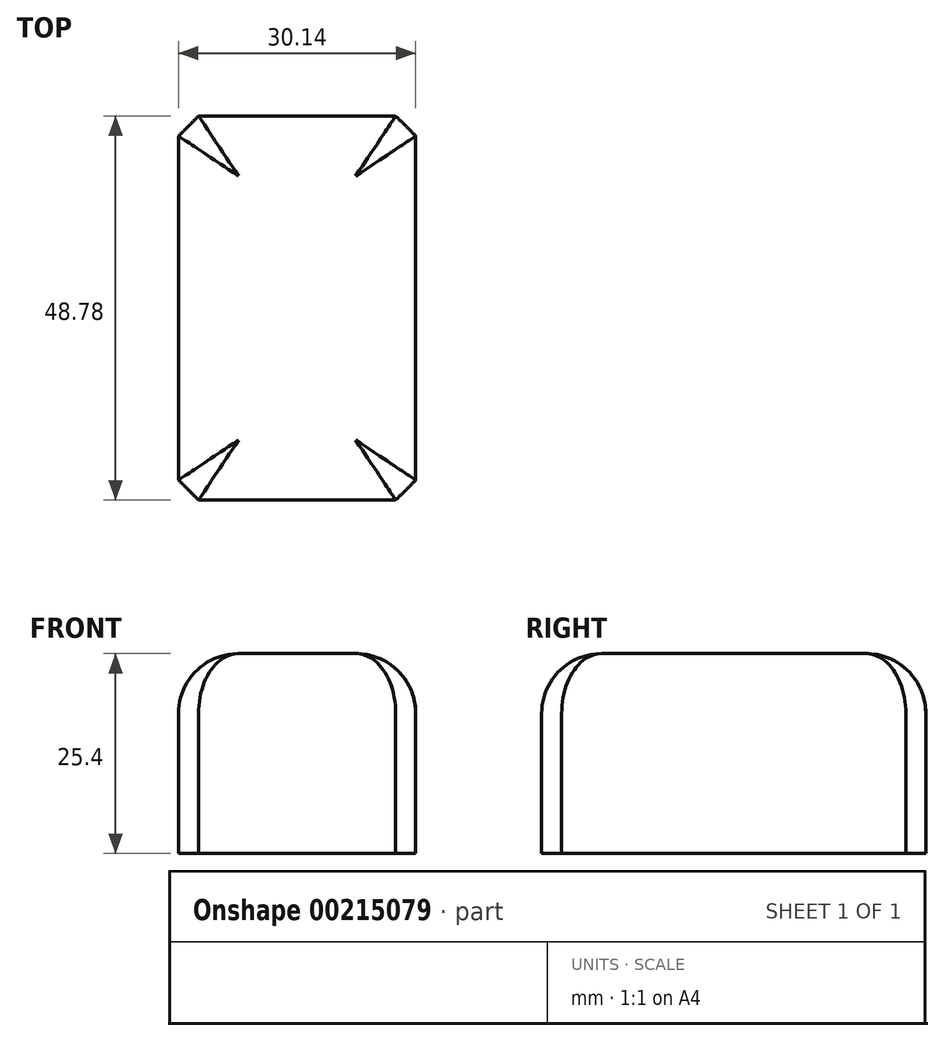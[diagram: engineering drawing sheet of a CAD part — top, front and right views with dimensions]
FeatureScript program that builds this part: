
annotation { "Feature Type Name" : "Feature", "Feature Type Description" : "" }
export const myFeature = defineFeature(function(context is Context, id is Id, definition is map)
    precondition{}
    {
        {
            var Q0;
            Q0=qCreatedBy(makeId("Top.planeOp"),FACE);
            var sketch = newSketch(context, id + "F2", { "sketchPlane" : qUnion([Q0])});
            skLineSegment(sketch, "E0.bottom", {"start": v(15.07, -24.4) * mm, "end": v(-15.07, -24.4) * mm});
            skLineSegment(sketch, "E0.top", {"start": v(15.07, 24.4) * mm, "end": v(-15.07, 24.4) * mm});
            skLineSegment(sketch, "E0.left", {"start": v(15.07, -24.4) * mm, "end": v(15.07, 24.4) * mm});
            skLineSegment(sketch, "E0.right", {"start": v(-15.07, -24.4) * mm, "end": v(-15.07, 24.4) * mm});
            skPoint(sketch, "E0.middle", {"position": v(0, 0) * mm});
            skSolve(sketch);
        }
        {
            var Q0;
            Q0=makeQuery(id+"F2.imprint","IMPRINT",FACE,{"disambiguationData":[TD([[makeQuery(id+"F2.imprint","IMPRINT",EDGE,{"derivedFrom":sQuery(id+"F2.wireOp",EDGE,"E0.bottom")}),-1.0]])]});
            extrude(context, id + "F0", {"entities" : qUnion([Q0]), "depth" : 25.4 * mm});
        }
        {
            var Q0;
            Q0=makeQuery(id+"F0.opExtrude","CAP_EDGE",EDGE,{"disambiguationData":[OSD([sQuery(id+"F2.wireOp",EDGE,"E0.left")])],"isStart":false});
            var Q1;
            Q1=makeQuery(id+"F0.opExtrude","CAP_EDGE",EDGE,{"disambiguationData":[OSD([sQuery(id+"F2.wireOp",EDGE,"E0.top")])],"isStart":false});
            var Q2;
            Q2=makeQuery(id+"F0.opExtrude","CAP_EDGE",EDGE,{"disambiguationData":[OSD([sQuery(id+"F2.wireOp",EDGE,"E0.right")])],"isStart":false});
            var Q3;
            Q3=makeQuery(id+"F0.opExtrude","CAP_EDGE",EDGE,{"disambiguationData":[OSD([sQuery(id+"F2.wireOp",EDGE,"E0.bottom")])],"isStart":false});
            fillet(context, id + "F1", {"entities" : qUnion([Q0, Q1, Q2, Q3]), "radius" : 7.62 * mm, "tangentPropagation" : true, "allowEdgeOverflow" : false});
        }
        {
            var Q0;
            Q0=makeQuery(id+"F0.opExtrude","SWEPT_EDGE",EDGE,{"disambiguationData":[OSD([sQuery(id+"F2.wireOp",EDGE,"E0.bottom"),sQuery(id+"F2.wireOp",EDGE,"E0.left")])]});
            var Q1;
            Q1=makeQuery(id+"F0.opExtrude","SWEPT_EDGE",EDGE,{"disambiguationData":[OSD([sQuery(id+"F2.wireOp",EDGE,"E0.bottom"),sQuery(id+"F2.wireOp",EDGE,"E0.right")])]});
            var Q2;
            Q2=makeQuery(id+"F0.opExtrude","SWEPT_EDGE",EDGE,{"disambiguationData":[OSD([sQuery(id+"F2.wireOp",EDGE,"E0.top"),sQuery(id+"F2.wireOp",EDGE,"E0.left")])]});
            var Q3;
            Q3=makeQuery(id+"F0.opExtrude","SWEPT_EDGE",EDGE,{"disambiguationData":[OSD([sQuery(id+"F2.wireOp",EDGE,"E0.top"),sQuery(id+"F2.wireOp",EDGE,"E0.right")])]});
            chamfer(context, id + "F3", {"entities" : qUnion([Q0, Q1, Q2, Q3]), "width" : 2.54 * mm, "tangentPropagation" : true});
        }
    });
